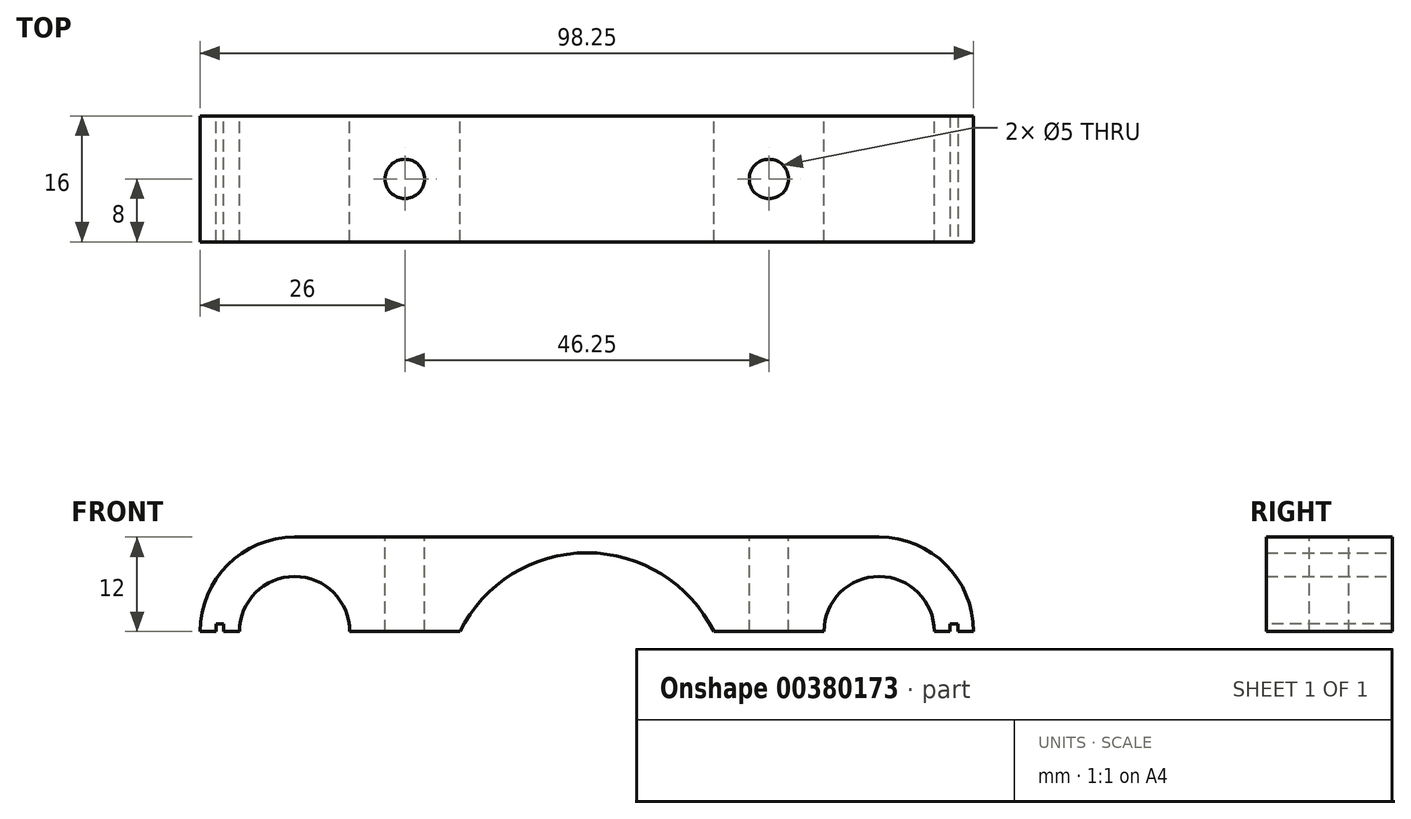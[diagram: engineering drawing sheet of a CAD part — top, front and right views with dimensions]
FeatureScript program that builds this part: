
annotation { "Feature Type Name" : "Feature", "Feature Type Description" : "" }
export const myFeature = defineFeature(function(context is Context, id is Id, definition is map)
    precondition{}
    {
        {
            var Q0;
            Q0=qCreatedBy(makeId("Front.planeOp"),FACE);
            var sketch = newSketch(context, id + "F0", { "sketchPlane" : qUnion([Q0])});
            skLineSegment(sketch, "E0", {"start": v(-33.25, -6) * mm, "end": v(-38.25, -6) * mm});
            skLineSegment(sketch, "E1", {"start": v(-38.25, -6) * mm, "end": v(-38.25, 6) * mm});
            skLineSegment(sketch, "E2", {"start": v(-38.25, 6) * mm, "end": v(60, 6) * mm});
            skLineSegment(sketch, "E3", {"start": v(60, 6) * mm, "end": v(60, -6) * mm});
            skLineSegment(sketch, "E4", {"start": v(60, -6) * mm, "end": v(55, -6) * mm});
            skArc(sketch, "E5", {"start": v(55, -6) * mm, "mid": v(48, 1) * mm, "end": v(41, -6) * mm});
            skArc(sketch, "E6", {"start": v(-19.25, -6) * mm, "mid": v(-26.25, 1) * mm, "end": v(-33.25, -6) * mm});
            skArc(sketch, "E7", {"start": v(27, -6) * mm, "mid": v(10.87, 4) * mm, "end": v(-5.25, -6) * mm});
            skLineSegment(sketch, "E8", {"start": v(-19.25, -6) * mm, "end": v(-5.25, -6) * mm});
            skLineSegment(sketch, "E9", {"start": v(27, -6) * mm, "end": v(41, -6) * mm});
            skSolve(sketch);
        }
        {
            var Q0;
            Q0=makeQuery(id+"F0.imprint","IMPRINT",FACE,{"disambiguationData":[TD([[makeQuery(id+"F0.imprint","IMPRINT",EDGE,{"derivedFrom":sQuery(id+"F0.wireOp",EDGE,"E0")}),-1.0]])]});
            extrude(context, id + "F1", {"entities" : qUnion([Q0]), "endBound" : BoundingType.SYMMETRIC, "depth" : 16 * mm});
        }
        {
            var Q0;
            Q0=makeQuery(id+"F1.opExtrude","SWEPT_FACE",FACE,{"disambiguationData":[OSD([sQuery(id+"F0.wireOp",EDGE,"E2")])]});
            var sketch = newSketch(context, id + "F2", { "sketchPlane" : qUnion([Q0])});
            skPoint(sketch, "E10", {"position": v(-12.25, 0) * mm});
            skPoint(sketch, "E11", {"position": v(34, 0) * mm});
            skSolve(sketch);
        }
        {
            var Q0;
            Q0=makeQuery(id+"F1.opExtrude","SWEPT_EDGE",EDGE,{"disambiguationData":[OSD([sQuery(id+"F0.wireOp",EDGE,"E1"),sQuery(id+"F0.wireOp",EDGE,"E2")])]});
            var Q1;
            Q1=makeQuery(id+"F1.opExtrude","SWEPT_EDGE",EDGE,{"disambiguationData":[OSD([sQuery(id+"F0.wireOp",EDGE,"E2"),sQuery(id+"F0.wireOp",EDGE,"E3")])]});
            fillet(context, id + "F3", {"entities" : qUnion([Q0, Q1]), "radius" : 12 * mm, "tangentPropagation" : true, "allowEdgeOverflow" : false});
        }
        {
            var Q0;
            Q0=sQuery(id+"F2.wireOp",VERTEX,"E10");
            var Q1;
            Q1=sQuery(id+"F2.wireOp",VERTEX,"E11");
            var Q2;
            Q2=makeQuery(id+"F1.opExtrude","SWEPT_BODY",BODY,{"disambiguationData":[OSD([sQuery(id+"F0.wireOp",EDGE,"E0"),sQuery(id+"F0.wireOp",EDGE,"E1"),sQuery(id+"F0.wireOp",EDGE,"E2"),sQuery(id+"F0.wireOp",EDGE,"E3"),sQuery(id+"F0.wireOp",EDGE,"E4"),sQuery(id+"F0.wireOp",EDGE,"E5"),sQuery(id+"F0.wireOp",EDGE,"E6"),sQuery(id+"F0.wireOp",EDGE,"IZRTLZFC-gH6G-mexX-SaW8-7kCsowfcQd4H")])]});
            hole(context, id + "F4", {"style" : HoleStyle.SIMPLE, "endStyle" : HoleEndStyle.THROUGH, "holeDiameter" : 5 * mm, "isTappedThrough" : true, "tappedDepth" : 12.7 * mm, "tapClearance" : 3, "locations" : qUnion([Q0, Q1]), "scope" : qUnion([Q2])});
        }
        {
            var Q0;
            Q0=makeQuery(id+"F1.opExtrude","SWEPT_FACE",FACE,{"disambiguationData":[OSD([sQuery(id+"F0.wireOp",EDGE,"E0")])]});
            var sketch = newSketch(context, id + "F5", { "sketchPlane" : qUnion([Q0])});
            skLineSegment(sketch, "E12.bottom", {"start": v(-36.25, 8) * mm, "end": v(-35.25, 8) * mm});
            skLineSegment(sketch, "E12.top", {"start": v(-36.25, -8) * mm, "end": v(-35.25, -8) * mm});
            skLineSegment(sketch, "E12.left", {"start": v(-36.25, 8) * mm, "end": v(-36.25, -8) * mm});
            skLineSegment(sketch, "E12.right", {"start": v(-35.25, 8) * mm, "end": v(-35.25, -8) * mm});
            skLineSegment(sketch, "E13.bottom", {"start": v(57, -8) * mm, "end": v(58, -8) * mm});
            skLineSegment(sketch, "E13.top", {"start": v(57, 8) * mm, "end": v(58, 8) * mm});
            skLineSegment(sketch, "E13.left", {"start": v(57, -8) * mm, "end": v(57, 8) * mm});
            skLineSegment(sketch, "E13.right", {"start": v(58, -8) * mm, "end": v(58, 8) * mm});
            skSolve(sketch);
        }
        {
            var Q0;
            Q0=makeQuery(id+"F5.imprint","IMPRINT",FACE,{"disambiguationData":[TD([[makeQuery(id+"F5.imprint","IMPRINT",EDGE,{"derivedFrom":sQuery(id+"F5.wireOp",EDGE,"E12.bottom")}),1.0]])]});
            var Q1;
            Q1=makeQuery(id+"F5.imprint","IMPRINT",FACE,{"disambiguationData":[TD([[makeQuery(id+"F5.imprint","IMPRINT",EDGE,{"derivedFrom":sQuery(id+"F5.wireOp",EDGE,"E13.bottom")}),1.0]])]});
            extrude(context, id + "F6", {"entities" : qUnion([Q0, Q1]), "operationType" : NewBodyOperationType.REMOVE, "oppositeDirection" : true, "depth" : 1 * mm, "offsetDistance" : 25 * mm});
        }
    });
